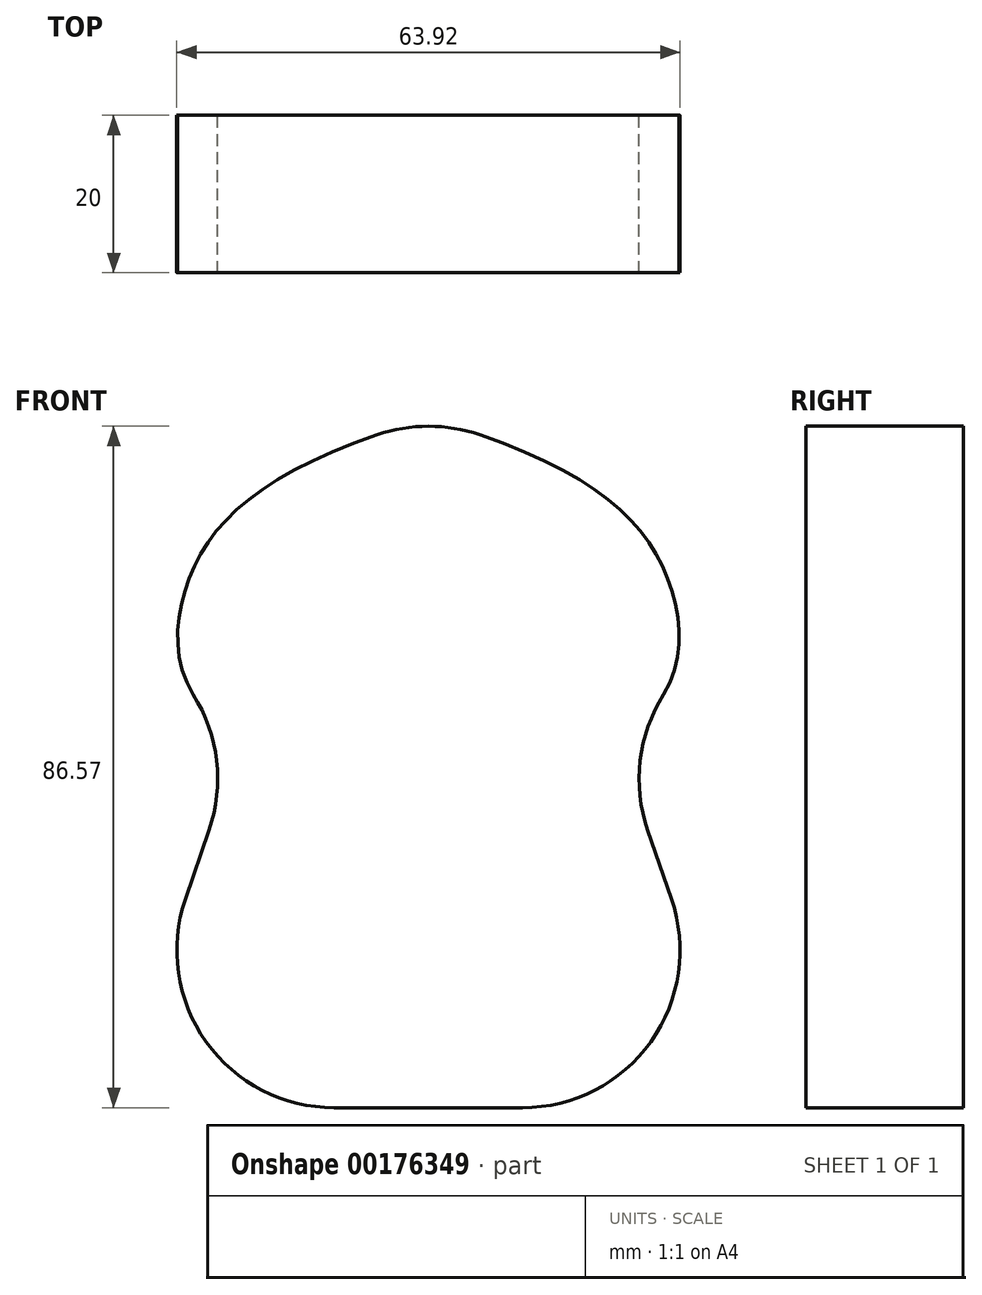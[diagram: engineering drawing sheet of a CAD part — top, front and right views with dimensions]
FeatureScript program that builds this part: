
annotation { "Feature Type Name" : "Feature", "Feature Type Description" : "" }
export const myFeature = defineFeature(function(context is Context, id is Id, definition is map)
    precondition{}
    {
        {
            var Q0;
            Q0=qCreatedBy(makeId("Front.planeOp"),FACE);
            var sketch = newSketch(context, id + "F0", { "sketchPlane" : qUnion([Q0])});
            skLineSegment(sketch, "E0", {"start": v(-23.72, -0.06) * mm, "end": v(-40, -47.33) * mm});
            skLineSegment(sketch, "E1", {"start": v(-40, -47.33) * mm, "end": v(0, -47.33) * mm});
            skFitSpline(sketch, "E2", {"points": [v(-23.72, -0.06) * mm, v(-30.88, 18.46) * mm, v(0, 40.17) * mm], "startDerivative": vector(-60.97, 29) * mm, "endDerivative": vector(104.04, 29.38) * mm});
            skLineSegment(sketch, "E3", {"start": v(0, 40.17) * mm, "end": v(0, -47.33) * mm, "construction": true});
            skFitSpline(sketch, "E4.MirrorCS", {"points": [v(23.72, -0.06) * mm, v(30.88, 18.46) * mm, v(0, 40.17) * mm], "startDerivative": vector(60.97, 29) * mm, "endDerivative": vector(-104.04, 29.38) * mm});
            skLineSegment(sketch, "E5.MirrorCS", {"start": v(23.72, -0.06) * mm, "end": v(40, -47.33) * mm});
            skLineSegment(sketch, "E6.MirrorCS", {"start": v(40, -47.33) * mm, "end": v(0, -47.33) * mm});
            skSolve(sketch);
        }
        {
            var Q0;
            Q0=makeQuery(id+"F0.imprint","IMPRINT",FACE,{"disambiguationData":[TD([[makeQuery(id+"F0.imprint","IMPRINT",EDGE,{"derivedFrom":sQuery(id+"F0.wireOp",EDGE,"E0")}),1.0]])]});
            extrude(context, id + "F1", {"entities" : qUnion([Q0]), "depth" : 20 * mm});
        }
        {
            var Q0;
            Q0=makeQuery(id+"F1.opExtrude","SWEPT_EDGE",EDGE,{"disambiguationData":[OSD([sQuery(id+"F0.wireOp",EDGE,"E2"),sQuery(id+"F0.wireOp",EDGE,"E4.MirrorCS")])]});
            var Q1;
            Q1=makeQuery(id+"F1.opExtrude","SWEPT_EDGE",EDGE,{"disambiguationData":[OSD([sQuery(id+"F0.wireOp",EDGE,"E5.MirrorCS"),sQuery(id+"F0.wireOp",EDGE,"E6.MirrorCS")])]});
            var Q2;
            Q2=makeQuery(id+"F1.opExtrude","SWEPT_EDGE",EDGE,{"disambiguationData":[OSD([sQuery(id+"F0.wireOp",EDGE,"E0"),sQuery(id+"F0.wireOp",EDGE,"E2")])]});
            var Q3;
            Q3=makeQuery(id+"F1.opExtrude","SWEPT_EDGE",EDGE,{"disambiguationData":[OSD([sQuery(id+"F0.wireOp",EDGE,"E4.MirrorCS"),sQuery(id+"F0.wireOp",EDGE,"E5.MirrorCS")])]});
            var Q4;
            Q4=makeQuery(id+"F1.opExtrude","SWEPT_EDGE",EDGE,{"disambiguationData":[OSD([sQuery(id+"F0.wireOp",EDGE,"E0"),sQuery(id+"F0.wireOp",EDGE,"E1")])]});
            fillet(context, id + "F2", {"entities" : qUnion([Q0, Q1, Q2, Q3, Q4]), "radius" : 20 * mm, "tangentPropagation" : true, "allowEdgeOverflow" : false});
        }
    });
